# Revit family: Shower-Asura-Trench-XST6236TR-COLHS-Seat
name_source: partatom
category: Plumbing Fixtures
units: mm (PartAtom-declared; Revit-internal decimal feet)

## family parameters
Always vertical = Yes
Cut with Voids When Loaded = No
OmniClass Number = 23.45.05.14.17
OmniClass Title = Showers
Part Type = Normal
Room Calculation Point = No
Round Connector Dimension = Use Radius
Shared = No
Work Plane-Based = No

## types (1)
- XST6236TR COL (HS)  With Seat
    1.125 Thershold = No
    ADA Compliant = Yes
    ANSI Compliant = Yes
    Assembly Code = D2010710
    Back Grab Bar = Yes
    Back Grab Bar Length = 2' - 8"
    Back Valve = Yes
    Back Valve Offset = 2' - 2"
    COL Threshold = Yes
    Connector Description = Asura Trench Drain Connection
    Default Elevation = 0' - 0"
    Depth = 3' - 0 1/8"
    Description = Roll-In Shower
    Drain Offset = 0' - 5 1/2"
    Drain Radius = 0' - 1 5/8"
    Finish = Gelcoat-Asura-White-Tile
    Grab Bar Height = 2' - 9 5/8"
    Hardware Finish = Metal-Stainless_Steel-Asura
    Height = 7' - 7"
    Interior Depth = 2' - 10"
    Interior Height = 7' - 6"
    Interior Width = 5' - 0"
    L Shape Grab Bar = No
    Left Grab Bar = Yes
    Lower Soap = Yes
    Lower Soap Offset = 2' - 0"
    Manufacturer = Asura Trench Drain
    Model = XST6236TR COL (HS)
    Outer Flange = 0' - 1 1/8"
    Product Documentation Link = http://www.asuratrench.com
    Product Page URL = http://www.asuratrench.com
    Right Grab Bar = No
    Seat = Yes
    Seat Finish = Gelcoat-Asura-White
    Seat Height = 1' - 5 7/8"
    Seat Width = 2' - 6"
    Side Grab Bar Length = 2' - 0"
    Side Valve = No
    Side Valve Offset = 1' - 6"
    Smooth Finish = Gelcoat-Asura-White
    Supply Connector Radius = 0' - 0 1/2"
    Threshold Height = 0' - 1"
    Trench = Metal-Stainless_Steel-Asura-Trench
    Trench Width = 0' - 5 1/2"
    Type Comments = Change of Level Threshold
    URL = http://www.asuratrench.com
    Upper Soap = Yes
    Upper Soap Offset = 1' - 3"
    Valve Height = 3' - 6"
    Vertical Grab Bar = No
    Width = 5' - 6"

## geometry (parser evidence)
native form markers: Blend x12, Sweep x10
no freeform markers — native parametric forms only
